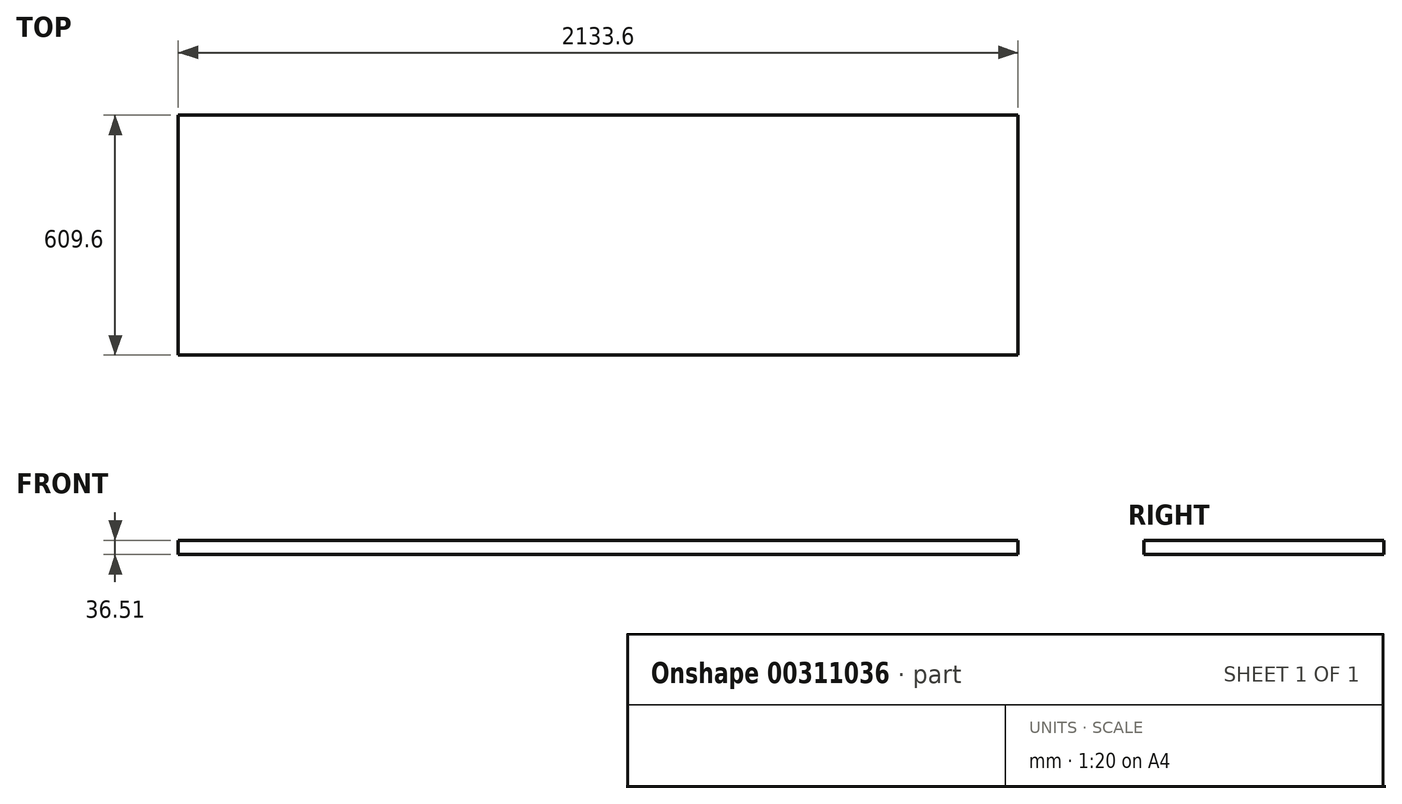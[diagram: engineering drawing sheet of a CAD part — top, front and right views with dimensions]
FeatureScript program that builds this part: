
annotation { "Feature Type Name" : "Feature", "Feature Type Description" : "" }
export const myFeature = defineFeature(function(context is Context, id is Id, definition is map)
    precondition{}
    {
        {
            var Q0;
            Q0=qCreatedBy(makeId("Top.planeOp"),FACE);
            var sketch = newSketch(context, id + "F0", { "sketchPlane" : qUnion([Q0])});
            skLineSegment(sketch, "E0.bottom", {"start": v(-1064.11, 92.94) * mm, "end": v(1069.49, 92.94) * mm});
            skLineSegment(sketch, "E0.top", {"start": v(-1064.11, -516.66) * mm, "end": v(1069.49, -516.66) * mm});
            skLineSegment(sketch, "E0.left", {"start": v(-1064.11, 92.94) * mm, "end": v(-1064.11, -516.66) * mm});
            skLineSegment(sketch, "E0.right", {"start": v(1069.49, 92.94) * mm, "end": v(1069.49, -516.66) * mm});
            skSolve(sketch);
        }
        {
            var Q0;
            Q0 = qSketchRegion(id + "F0", true);
            extrude(context, id + "F1", {"entities" : qUnion([Q0]), "depth" : 36.5 * mm});
        }
    });
